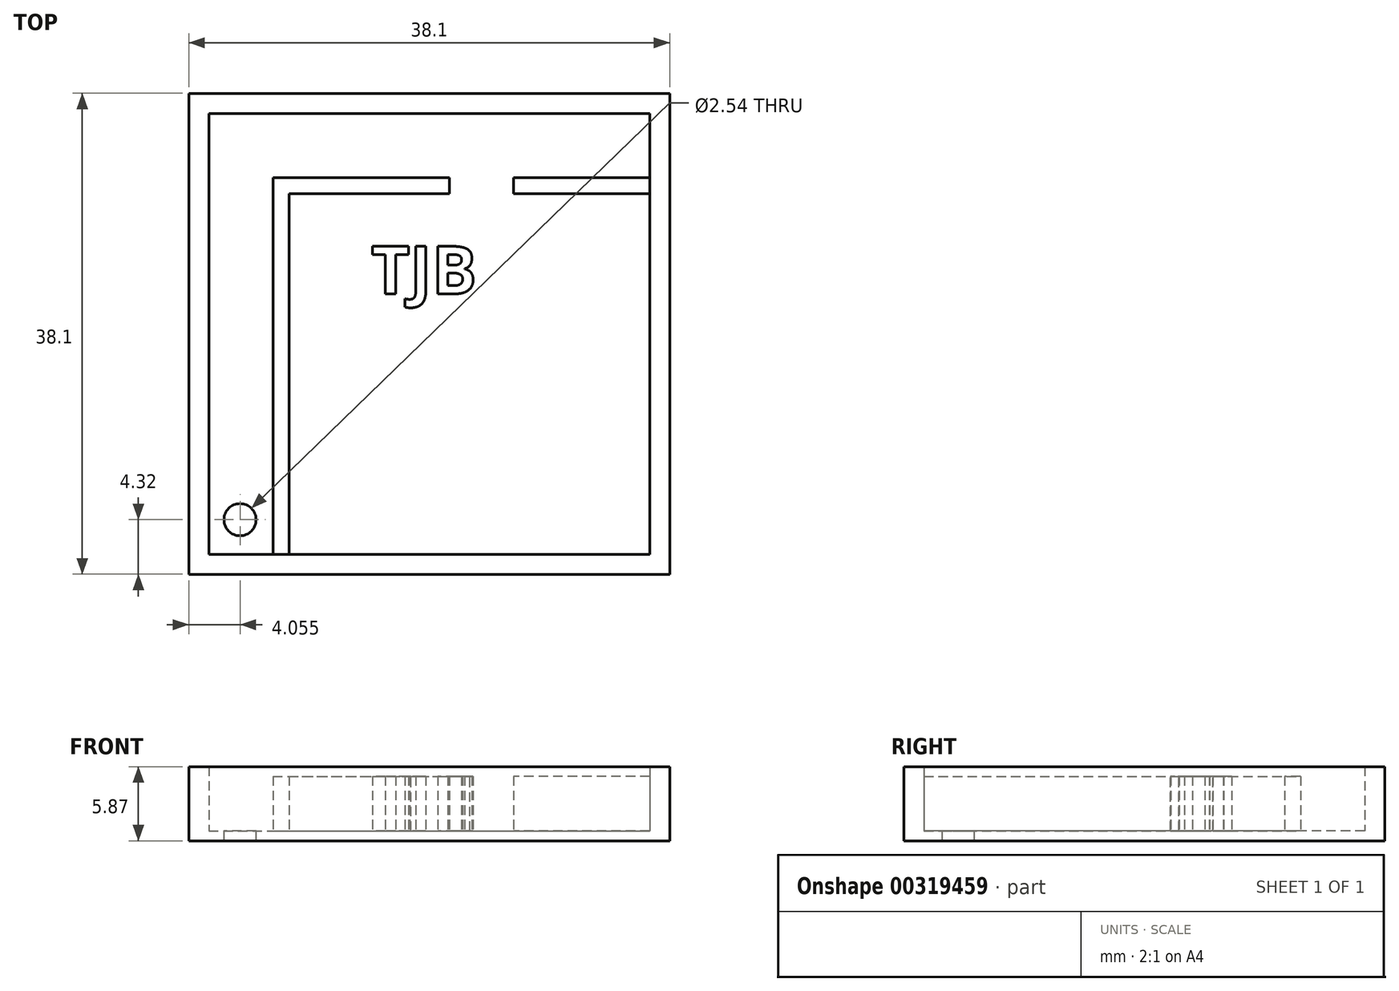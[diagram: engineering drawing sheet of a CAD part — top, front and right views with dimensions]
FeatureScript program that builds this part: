
annotation { "Feature Type Name" : "Feature", "Feature Type Description" : "" }
export const myFeature = defineFeature(function(context is Context, id is Id, definition is map)
    precondition{}
    {
        {
            var Q0;
            Q0=qCreatedBy(makeId("Top.planeOp"),FACE);
            var sketch = newSketch(context, id + "F0", { "sketchPlane" : qUnion([Q0])});
            skLineSegment(sketch, "E0.bottom", {"start": v(13.95, -22.23) * mm, "end": v(52.05, -22.23) * mm});
            skLineSegment(sketch, "E0.top", {"start": v(13.95, -60.33) * mm, "end": v(52.05, -60.33) * mm});
            skLineSegment(sketch, "E0.left", {"start": v(13.95, -22.23) * mm, "end": v(13.95, -60.33) * mm});
            skLineSegment(sketch, "E0.right", {"start": v(52.05, -22.23) * mm, "end": v(52.05, -60.33) * mm});
            skSolve(sketch);
        }
        {
            var Q0;
            Q0=makeQuery(id+"F0.imprint","IMPRINT",FACE,{"disambiguationData":[TD([[makeQuery(id+"F0.imprint","IMPRINT",EDGE,{"derivedFrom":sQuery(id+"F0.wireOp",EDGE,"E0.bottom")}),-1.0]])]});
            extrude(context, id + "F1", {"entities" : qUnion([Q0]), "depth" : 0.8 * mm});
        }
        {
            var Q0;
            Q0=makeQuery(id+"F1.opExtrude","CAP_FACE",FACE,{"disambiguationData":[OSD([sQuery(id+"F0.wireOp",EDGE,"E0.bottom"),sQuery(id+"F0.wireOp",EDGE,"E0.top"),sQuery(id+"F0.wireOp",EDGE,"E0.left"),sQuery(id+"F0.wireOp",EDGE,"E0.right")])],"isStart":false});
            var sketch = newSketch(context, id + "F2", { "sketchPlane" : qUnion([Q0])});
            skLineSegment(sketch, "E1.0", {"start": v(15.54, -23.82) * mm, "end": v(50.46, -23.82) * mm});
            skLineSegment(sketch, "E1.1", {"start": v(15.54, -23.82) * mm, "end": v(15.54, -58.75) * mm});
            skLineSegment(sketch, "E1.2", {"start": v(15.54, -58.75) * mm, "end": v(50.46, -58.75) * mm});
            skLineSegment(sketch, "E1.3", {"start": v(50.46, -23.82) * mm, "end": v(50.46, -58.75) * mm});
            skSolve(sketch);
        }
        {
            var Q0;
            Q0=makeQuery(id+"F2.imprint","IMPRINT",FACE,{"disambiguationData":[TD([[makeQuery(id+"F2.imprint","IMPRINT",EDGE,{"derivedFrom":sQuery(id+"F2.wireOp",EDGE,"E1.0")}),1.0]])]});
            extrude(context, id + "F3", {"entities" : qUnion([Q0]), "operationType" : NewBodyOperationType.ADD, "depth" : 5.08 * mm, "offsetDistance" : 25.4 * mm});
        }
        {
            var Q0;
            Q0=makeQuery(id+"F1.opExtrude","CAP_FACE",FACE,{"disambiguationData":[OSD([sQuery(id+"F0.wireOp",EDGE,"E0.bottom"),sQuery(id+"F0.wireOp",EDGE,"E0.top"),sQuery(id+"F0.wireOp",EDGE,"E0.left"),sQuery(id+"F0.wireOp",EDGE,"E0.right")])],"isStart":false});
            var sketch = newSketch(context, id + "F4", { "sketchPlane" : qUnion([Q0])});
            skLineSegment(sketch, "E2.bottom", {"start": v(20.62, -58.75) * mm, "end": v(21.89, -58.75) * mm});
            skLineSegment(sketch, "E2.left", {"start": v(20.62, -58.75) * mm, "end": v(20.62, -28.9) * mm});
            skLineSegment(sketch, "E2.right", {"start": v(21.89, -58.75) * mm, "end": v(21.89, -30.17) * mm});
            skLineSegment(sketch, "E3.top", {"start": v(21.89, -30.17) * mm, "end": v(34.59, -30.17) * mm});
            skLineSegment(sketch, "E3.right", {"start": v(34.59, -28.9) * mm, "end": v(34.59, -30.17) * mm});
            skLineSegment(sketch, "E4", {"start": v(20.62, -28.9) * mm, "end": v(34.59, -28.9) * mm});
            skLineSegment(sketch, "E5.bottom", {"start": v(50.46, -28.9) * mm, "end": v(39.67, -28.9) * mm});
            skLineSegment(sketch, "E5.top", {"start": v(50.46, -30.17) * mm, "end": v(39.67, -30.17) * mm});
            skLineSegment(sketch, "E5.left", {"start": v(50.46, -28.9) * mm, "end": v(50.46, -30.17) * mm});
            skLineSegment(sketch, "E5.right", {"start": v(39.67, -28.9) * mm, "end": v(39.67, -30.17) * mm});
            skLineSegment(sketch, "E6.bottom", {"start": v(27.96, -36.05) * mm, "end": v(29.47, -36.05) * mm});
            skLineSegment(sketch, "E6.top", {"start": v(27.96, -52.09) * mm, "end": v(29.47, -52.09) * mm});
            skLineSegment(sketch, "E6.left", {"start": v(27.96, -36.05) * mm, "end": v(27.96, -40.06) * mm});
            skLineSegment(sketch, "E6.right", {"start": v(29.47, -36.05) * mm, "end": v(29.47, -40.06) * mm});
            skLineSegment(sketch, "E7.bottom", {"start": v(24.7, -40.06) * mm, "end": v(27.96, -40.06) * mm});
            skLineSegment(sketch, "E7.top", {"start": v(24.7, -41.91) * mm, "end": v(27.96, -41.91) * mm});
            skLineSegment(sketch, "E7.left", {"start": v(24.7, -40.06) * mm, "end": v(24.7, -41.91) * mm});
            skLineSegment(sketch, "E7.right", {"start": v(40.04, -40.06) * mm, "end": v(40.04, -41.91) * mm});
            skLineSegment(sketch, "E8.trimOffspring", {"start": v(29.47, -40.06) * mm, "end": v(40.04, -40.06) * mm});
            skLineSegment(sketch, "E9.trimOffspring", {"start": v(27.96, -41.91) * mm, "end": v(27.96, -52.09) * mm});
            skLineSegment(sketch, "E10.trimOffspring", {"start": v(29.47, -41.91) * mm, "end": v(40.04, -41.91) * mm});
            skLineSegment(sketch, "E11.trimOffspring", {"start": v(29.47, -41.91) * mm, "end": v(29.47, -52.09) * mm});
            skSolve(sketch);
        }
        {
            var Q0;
            Q0=makeQuery(id+"F4.imprint","IMPRINT",FACE,{"disambiguationData":[TD([[makeQuery(id+"F4.imprint","IMPRINT",EDGE,{"derivedFrom":sQuery(id+"F4.wireOp",EDGE,"E2.bottom")}),1.0]])]});
            var Q1;
            Q1=makeQuery(id+"F4.imprint","IMPRINT",FACE,{"disambiguationData":[TD([[makeQuery(id+"F4.imprint","IMPRINT",EDGE,{"derivedFrom":sQuery(id+"F4.wireOp",EDGE,"E5.bottom")}),1.0]])]});
            extrude(context, id + "F5", {"entities" : qUnion([Q0, Q1]), "operationType" : NewBodyOperationType.ADD, "depth" : 4.32 * mm, "offsetDistance" : 25.4 * mm});
        }
        {
            var Q0;
            {var subQ4=sQuery(id+"F4.wireOp",EDGE,"E2.left");Q0=makeQuery(id+"F4.imprint","IMPRINT",FACE,{"disambiguationData":[TD([[makeQuery(id+"F4.imprint","IMPRINT",EDGE,{"derivedFrom":subQ4}),1.0]])]});}
            var sketch = newSketch(context, id + "F6", { "sketchPlane" : qUnion([Q0])});
            skCircle(sketch, "E12", {"center": v(18, -56.01) * mm, "radius": 1.27 * mm});
            skSolve(sketch);
        }
        {
            var Q0;
            Q0=makeQuery(id+"F6.imprint","IMPRINT",FACE,{"disambiguationData":[TD([[makeQuery(id+"F6.imprint","IMPRINT",EDGE,{"derivedFrom":sQuery(id+"F6.wireOp",EDGE,"E12")}),1.0]])]});
            extrude(context, id + "F7", {"entities" : qUnion([Q0]), "operationType" : NewBodyOperationType.REMOVE, "endBound" : BoundingType.THROUGH_ALL, "oppositeDirection" : true, "depth" : 25.4 * mm, "offsetDistance" : 25.4 * mm});
        }
        {
            var Q0;
            {var subQ4=sQuery(id+"F4.wireOp",EDGE,"E2.left");Q0=makeQuery(id+"F4.imprint","IMPRINT",FACE,{"disambiguationData":[TD([[makeQuery(id+"F4.imprint","IMPRINT",EDGE,{"derivedFrom":subQ4}),1.0]])]});}
            var sketch = newSketch(context, id + "F8", { "sketchPlane" : qUnion([Q0])});
            skText(sketch, "E13", { "text": "TJB", "fontName": "OpenSans-Bold.ttf"});
            const initialGuessF8  = {"E13": [0.0284, -0.03812, 1, 0, 0.0038]};
            skSetInitialGuess(sketch, initialGuessF8);
            skSolve(sketch);
        }
        {
            var Q0;
            Q0 = qSketchRegion(id + "F8", true);
            extrude(context, id + "F9", {"entities" : qUnion([Q0]), "operationType" : NewBodyOperationType.ADD, "depth" : 4.32 * mm, "offsetDistance" : 25.4 * mm});
        }
    });
